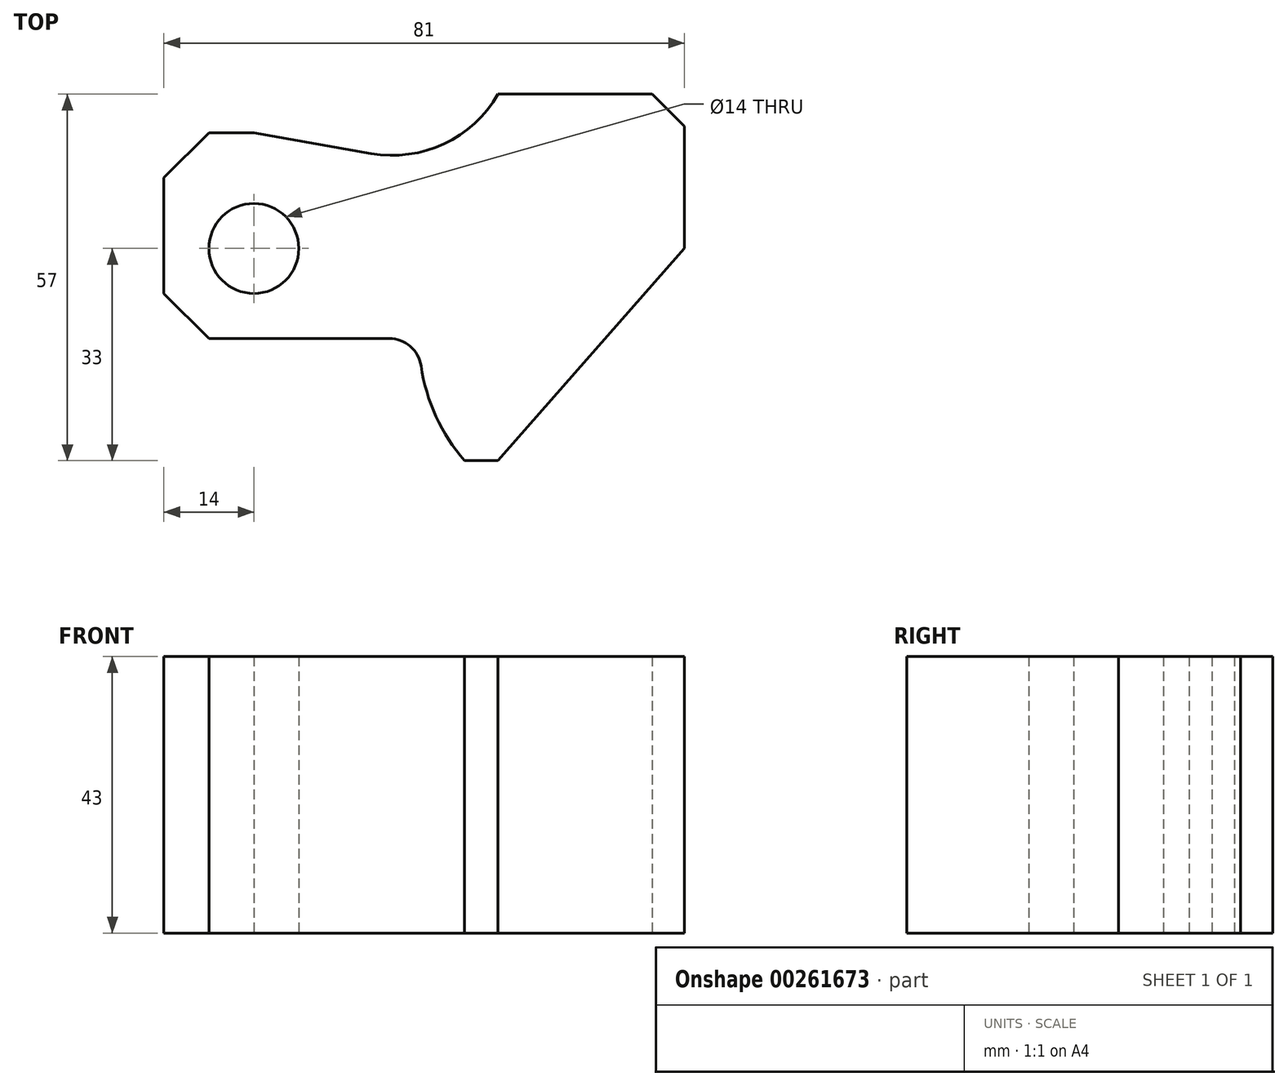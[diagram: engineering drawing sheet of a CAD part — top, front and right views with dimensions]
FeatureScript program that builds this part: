
annotation { "Feature Type Name" : "Feature", "Feature Type Description" : "" }
export const myFeature = defineFeature(function(context is Context, id is Id, definition is map)
    precondition{}
    {
        {
            var Q0;
            Q0=qCreatedBy(makeId("Top.planeOp"),FACE);
            var sketch = newSketch(context, id + "F0", { "sketchPlane" : qUnion([Q0])});
            skPoint(sketch, "E0.middle", {"position": v(0, 0) * mm});
            skLineSegment(sketch, "E1", {"start": v(-14, -7) * mm, "end": v(-7, -14) * mm});
            skLineSegment(sketch, "E2", {"start": v(-7, -14) * mm, "end": v(-7, -14) * mm});
            skLineSegment(sketch, "E3", {"start": v(-14, 11) * mm, "end": v(-7, 18) * mm});
            skLineSegment(sketch, "E4", {"start": v(-14, 11) * mm, "end": v(-14, -7) * mm});
            skLineSegment(sketch, "E5", {"start": v(-7, 18) * mm, "end": v(0, 18) * mm});
            skLineSegment(sketch, "E6", {"start": v(-7, -14) * mm, "end": v(0, -14) * mm});
            skCircle(sketch, "E7", {"center": v(0, 0) * mm, "radius": 7 * mm});
            skLineSegment(sketch, "E8", {"start": v(0, 18) * mm, "end": v(18.24, 14.78) * mm});
            skArc(sketch, "E9", {"start": v(18.24, 14.78) * mm, "mid": v(29.57, 16.28) * mm, "end": v(38, 24) * mm});
            skLineSegment(sketch, "E10", {"start": v(0, 10.36) * mm, "end": v(0, -17.57) * mm, "construction": true});
            skLineSegment(sketch, "E11", {"start": v(-18.76, 0) * mm, "end": v(13.25, 0) * mm, "construction": true});
            skLineSegment(sketch, "E12", {"start": v(0, 0) * mm, "end": v(0, -14) * mm});
            skLineSegment(sketch, "E13", {"start": v(38, 24) * mm, "end": v(62, 24) * mm});
            skLineSegment(sketch, "E14", {"start": v(62, 24) * mm, "end": v(67, 19) * mm});
            skLineSegment(sketch, "E15", {"start": v(67, 19) * mm, "end": v(67, 0) * mm});
            skLineSegment(sketch, "E16", {"start": v(67, 0) * mm, "end": v(38, -33) * mm});
            skLineSegment(sketch, "E17", {"start": v(0, -14) * mm, "end": v(21.07, -14) * mm});
            skLineSegment(sketch, "E18", {"start": v(38, -33) * mm, "end": v(32.79, -33) * mm});
            skArc(sketch, "E19", {"start": v(26.01, -18.26) * mm, "mid": v(24.33, -15.21) * mm, "end": v(21.07, -14) * mm});
            skArc(sketch, "E20", {"start": v(26.01, -18.26) * mm, "mid": v(28.35, -26.12) * mm, "end": v(32.79, -33) * mm});
            skLineSegment(sketch, "E21", {"start": v(67, 19) * mm, "end": v(67, 40.52) * mm, "construction": true});
            skLineSegment(sketch, "E22", {"start": v(-14, 11) * mm, "end": v(-14, 32.51) * mm, "construction": true});
            skLineSegment(sketch, "E23", {"start": v(-14, -7) * mm, "end": v(-14, -23.99) * mm, "construction": true});
            skSolve(sketch);
        }
        {
            var Q0;
            Q0=makeQuery(id+"F0.imprint","IMPRINT",FACE,{"disambiguationData":[TD([[makeQuery(id+"F0.imprint","IMPRINT",EDGE,{"derivedFrom":sQuery(id+"F0.wireOp",EDGE,"E1")}),1.0]])]});
            extrude(context, id + "F1", {"entities" : qUnion([Q0]), "depth" : 43 * mm});
        }
    });
